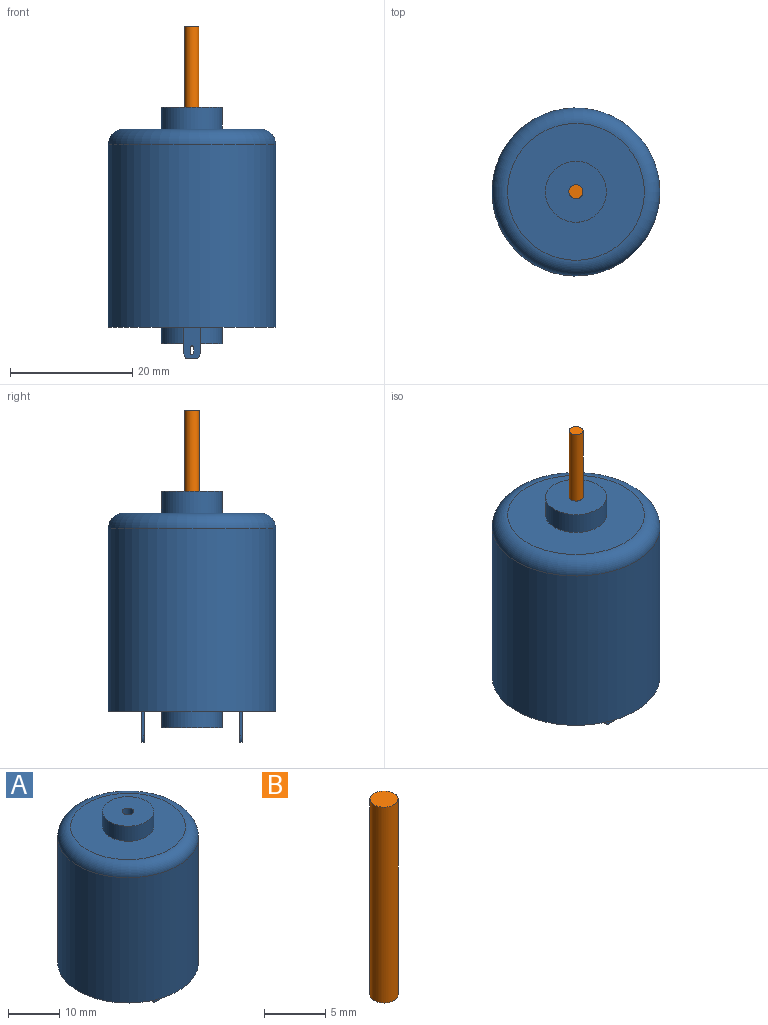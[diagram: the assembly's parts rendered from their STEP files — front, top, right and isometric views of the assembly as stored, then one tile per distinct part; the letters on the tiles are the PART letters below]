
ASSEMBLY  parts=2 mates=1
PART A: 26 faces, bbox 29.8x29.8x41.1 mm
  f0: plane 3.95x0.4mm, normal (1,0,0), area 1.6mm2, adj f4,f5,f8,f23
  f1: plane 3.95x0.4mm, normal (-1,0,0), area 1.6mm2, adj f4,f5,f8,f22
  f2: plane 1.97x0.4mm, normal (0,0,-1), area 0.8mm2, adj f4,f5,f22,f23
  f3: plane 1.97x0.4mm, normal (0,0,-1), area 0.8mm2, adj f6,f7,f20,f21
  f4: plane 5x2.8mm, normal (0,-1,0), area 13mm2, adj f0,f1,f2,f8,f22,f23,f25
  f5: plane 5x2.8mm, normal (0,1,0), area 13mm2, adj f0,f1,f2,f8,f22,f23,f25
  f6: plane 5x2.8mm, normal (0,-1,0), area 13mm2, adj f3,f8,f18,f19,f20,f21,f24
  f7: plane 5x2.8mm, normal (0,1,0), area 13mm2, adj f3,f8,f18,f19,f20,f21,f24
  f8: plane 27.5x27.5mm, normal (0,0,-1), area 513.2mm2, adj f0,f1,f4,f5,f6,f7,f9,f14
  f9: cylinder r=13.75mm len=29.96mm, axis (0,0,-1), area 2588.4mm2, adj f8,f11
  f10: plane 22.42x22.42mm, normal (0,0,1), area 316.2mm2, adj f11,f12
  f11: torus R=11.21mm, axis (0,0,1), area 321.6mm2, adj f9,f10
  f12: cylinder r=5mm len=10mm, axis (0,0,-1), area 113.1mm2, adj f10,f13
  f13: plane 10x10mm, normal (0,0,1), area 74.4mm2, adj f12,f16
  f14: cylinder r=5mm len=10mm, axis (0,0,1), area 84.8mm2, adj f8,f15
  f15: plane 10x10mm, normal (0,0,-1), area 78.5mm2, adj f14
  f16: cylinder r=1.15mm len=6.35mm, axis (0,0,1), area 45.9mm2, adj f13,f17
  f17: plane 2.3x2.3mm, normal (0,0,1), area 4.2mm2, adj f16
  f18: plane 3.95x0.4mm, normal (1,0,0), area 1.6mm2, adj f6,f7,f8,f21
  f19: plane 3.95x0.4mm, normal (-1,0,0), area 1.6mm2, adj f6,f7,f8,f20
  f20: cylinder r=1.57mm len=1.05mm, axis (0,1,0), area 0.5mm2, adj f3,f6,f7,f19
  f21: cylinder r=1.57mm len=1.05mm, axis (0,1,0), area 0.5mm2, adj f3,f6,f7,f18
  f22: cylinder r=1.57mm len=1.05mm, axis (0,1,0), area 0.5mm2, adj f1,f2,f4,f5
  f23: cylinder r=1.57mm len=1.05mm, axis (0,1,0), area 0.5mm2, adj f0,f2,f4,f5
  f24: extruded ~1.51x0.63mm, area 1.4mm2, adj f6,f7
  f25: extruded ~1.51x0.63mm, area 1.4mm2, adj f4,f5
PART B: 3 faces, bbox 2.3x2.3x19.7 mm
  f0: cylinder r=1.15mm len=19.65mm, axis (0,0,-1), area 142mm2, adj f1,f2
  f1: plane 2.3x2.3mm, normal (0,0,1), area 4.2mm2, adj f0
  f2: plane 2.3x2.3mm, normal (0,0,-1), area 4.2mm2, adj f0
PLACE A at identity fixed
PLACE B rot(axis=(0,0,-1),179.7deg) t=(0,0,0)mm
MATE revolute B.f0 <-> A.f16  axis (0,0,-1) through (0,0,29.75)mm
